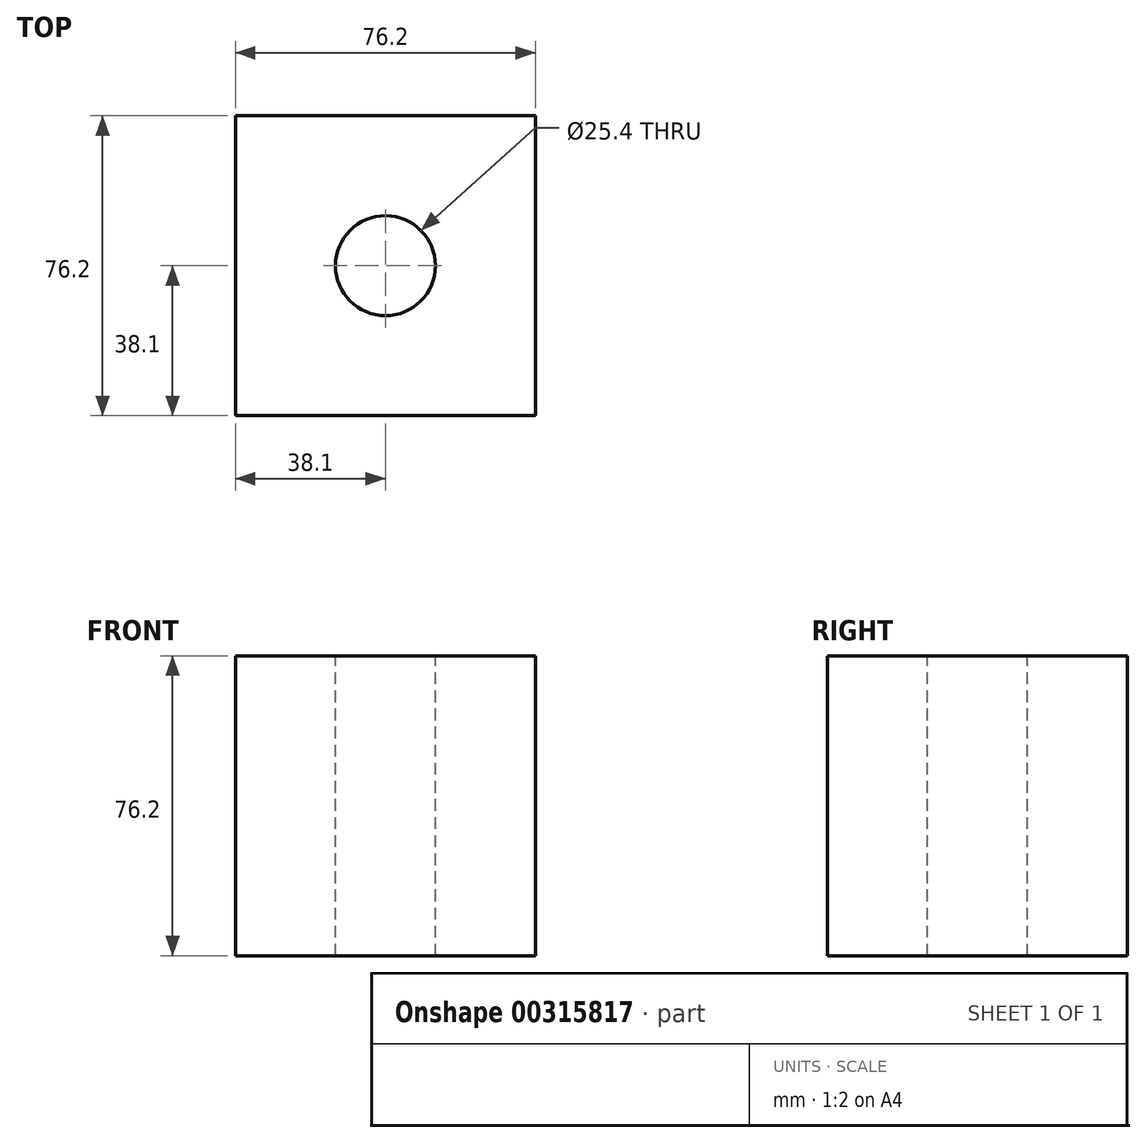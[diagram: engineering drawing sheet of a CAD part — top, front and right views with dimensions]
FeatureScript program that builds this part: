
annotation { "Feature Type Name" : "Feature", "Feature Type Description" : "" }
export const myFeature = defineFeature(function(context is Context, id is Id, definition is map)
    precondition{}
    {
        {
            var Q0;
            Q0=qCreatedBy(makeId("Top.planeOp"),FACE);
            var sketch = newSketch(context, id + "F0", { "sketchPlane" : qUnion([Q0])});
            skLineSegment(sketch, "E0.bottom", {"start": v(38.1, -38.1) * mm, "end": v(-38.1, -38.1) * mm});
            skLineSegment(sketch, "E0.top", {"start": v(38.1, 38.1) * mm, "end": v(-38.1, 38.1) * mm});
            skLineSegment(sketch, "E0.left", {"start": v(38.1, -38.1) * mm, "end": v(38.1, 38.1) * mm});
            skLineSegment(sketch, "E0.right", {"start": v(-38.1, -38.1) * mm, "end": v(-38.1, 38.1) * mm});
            skPoint(sketch, "E0.middle", {"position": v(0, 0) * mm});
            skSolve(sketch);
        }
        {
            var Q0;
            Q0=makeQuery(id+"F0.imprint","IMPRINT",FACE,{"disambiguationData":[TD([[makeQuery(id+"F0.imprint","IMPRINT",EDGE,{"derivedFrom":sQuery(id+"F0.wireOp",EDGE,"E0.bottom")}),-1.0]])]});
            var sketch = newSketch(context, id + "F1", { "sketchPlane" : qUnion([Q0])});
            skSolve(sketch);
        }
        {
            var Q0;
            Q0 = qSketchRegion(id + "F1", true);
            var Q1;
            Q1=makeQuery(id+"F1.imprint","IMPRINT",FACE,{"disambiguationData":[TD([[makeQuery(id+"F1.imprint","IMPRINT",EDGE,{"derivedFrom":makeQuery(id+"F0.imprint","IMPRINT",EDGE,{"derivedFrom":sQuery(id+"F0.wireOp",EDGE,"E0.bottom")})}),-1.0]])]});
            extrude(context, id + "F2", {"entities" : qUnion([Q0, Q1]), "depth" : 76.2 * mm});
        }
        {
            var Q0;
            Q0=makeQuery(id+"F2.opExtrude","CAP_FACE",FACE,{"disambiguationData":[OSD([sQuery(id+"F0.wireOp",EDGE,"E0.bottom"),sQuery(id+"F0.wireOp",EDGE,"E0.top"),sQuery(id+"F0.wireOp",EDGE,"E0.left"),sQuery(id+"F0.wireOp",EDGE,"E0.right")])],"isStart":false});
            var sketch = newSketch(context, id + "F3", { "sketchPlane" : qUnion([Q0])});
            skCircle(sketch, "E1", {"center": v(0, 0) * mm, "radius": 12.7 * mm});
            skSolve(sketch);
        }
        {
            var Q0;
            Q0=makeQuery(id+"F3.imprint","IMPRINT",FACE,{"disambiguationData":[TD([[makeQuery(id+"F3.imprint","IMPRINT",EDGE,{"derivedFrom":sQuery(id+"F3.wireOp",EDGE,"E1")}),1.0]])]});
            var Q1;
            Q1=sQuery(id+"F3.wireOp",EDGE,"E1");
            extrude(context, id + "F4", {"entities" : qUnion([Q0]), "operationType" : NewBodyOperationType.REMOVE, "surfaceEntities" : qUnion([Q1]), "endBound" : BoundingType.THROUGH_ALL, "oppositeDirection" : true, "depth" : 129.46 * mm});
        }
    });
